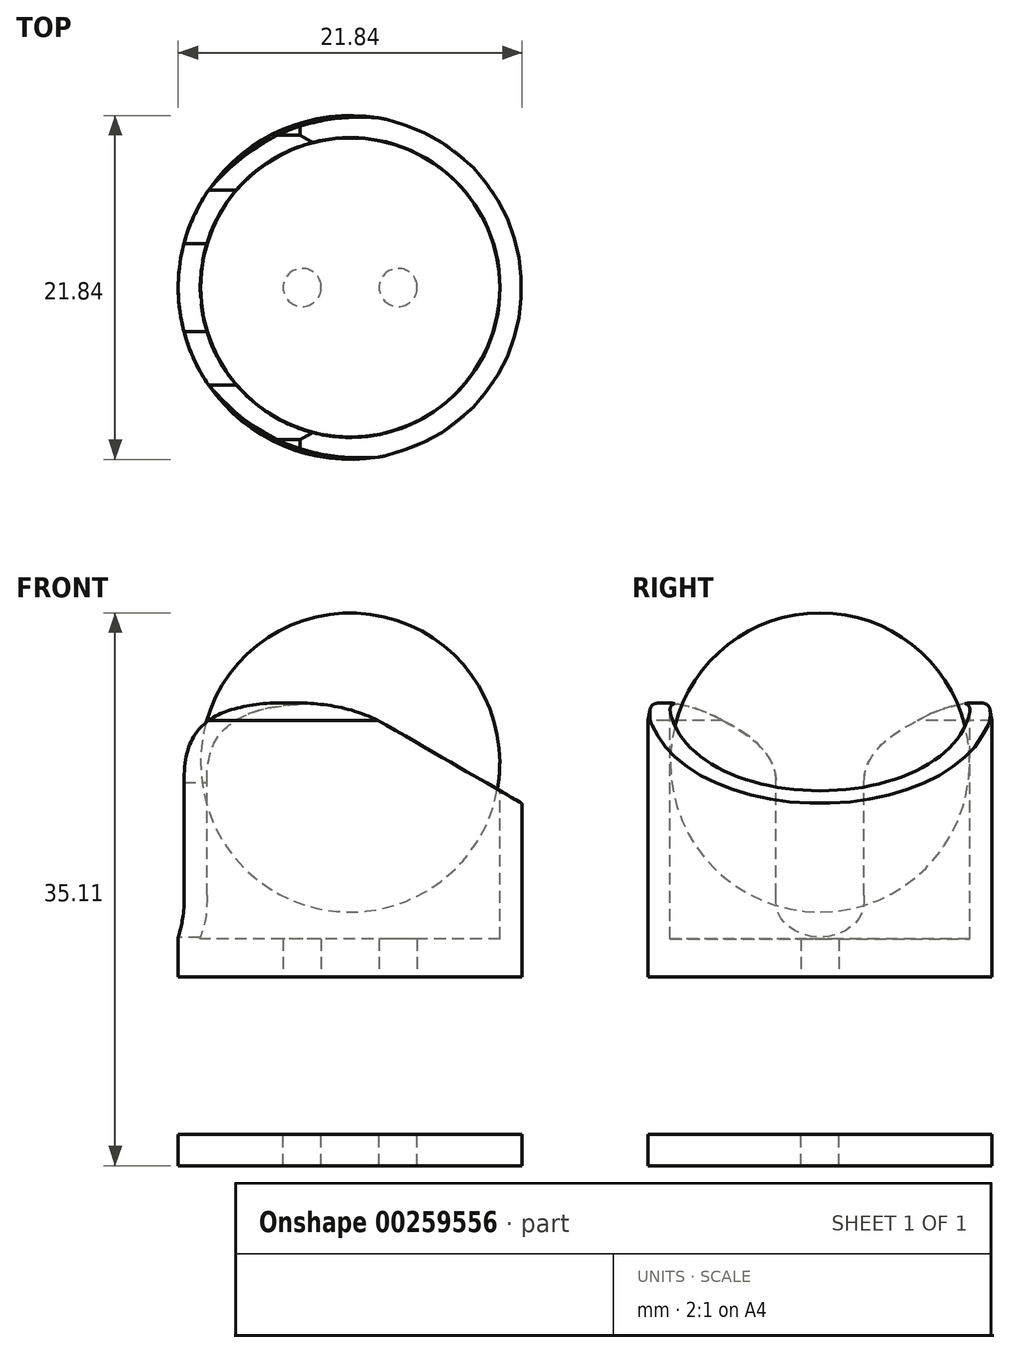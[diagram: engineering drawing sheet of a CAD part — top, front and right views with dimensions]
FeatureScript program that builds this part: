
annotation { "Feature Type Name" : "Feature", "Feature Type Description" : "" }
export const myFeature = defineFeature(function(context is Context, id is Id, definition is map)
    precondition{}
    {
        {
            var Q0;
            Q0=qCreatedBy(makeId("Top.planeOp"),FACE);
            var sketch = newSketch(context, id + "F0", { "sketchPlane" : qUnion([Q0])});
            skCircle(sketch, "E0", {"center": v(0, 0) * mm, "radius": 10.92 * mm});
            skCircle(sketch, "E1", {"center": v(-3.05, 0) * mm, "radius": 1.2 * mm});
            skCircle(sketch, "E2", {"center": v(3.05, 0) * mm, "radius": 1.2 * mm});
            skSolve(sketch);
        }
        {
            var Q0;
            Q0=makeQuery(id+"F0.imprint","IMPRINT",FACE,{"disambiguationData":[TD([[makeQuery(id+"F0.imprint","IMPRINT",EDGE,{"derivedFrom":sQuery(id+"F0.wireOp",EDGE,"E0")}),1.0]])]});
            extrude(context, id + "F1", {"entities" : qUnion([Q0]), "depth" : 17.4 * mm});
        }
        {
            var Q0;
            Q0=qCreatedBy(makeId("Front.planeOp"),FACE);
            var sketch = newSketch(context, id + "F2", { "sketchPlane" : qUnion([Q0])});
            skLineSegment(sketch, "E3.0", {"start": v(-10.92, 0) * mm, "end": v(10.92, 0) * mm});
            skLineSegment(sketch, "E4", {"start": v(10.92, 0) * mm, "end": v(10.92, 11) * mm});
            skLineSegment(sketch, "E5", {"start": v(10.92, 11) * mm, "end": v(2.26, 16) * mm});
            skLineSegment(sketch, "E6", {"start": v(-10.92, 0) * mm, "end": v(-10.92, 2.52) * mm});
            skFitSpline(sketch, "E7", {"points": [v(-10.92, 2.52) * mm, v(-10.63, 3.75) * mm, v(-10.56, 5.17) * mm], "startDerivative": vector(0.7, 2.47) * mm, "endDerivative": vector(0, 2.82) * mm});
            skLineSegment(sketch, "E8", {"start": v(-10.56, 5.17) * mm, "end": v(-10.56, 12.35) * mm});
            skFitSpline(sketch, "E9", {"points": [v(-10.56, 12.35) * mm, v(-9.97, 15.2) * mm, v(-7.3, 17.04) * mm, v(-0.9, 17.16) * mm, v(2.26, 16) * mm], "startDerivative": vector(0, 14.16) * mm, "endDerivative": vector(11.3, -6.52) * mm});
            skSolve(sketch);
        }
        {
            var Q0;
            Q0=makeQuery(id+"F1.opExtrude","CAP_EDGE",EDGE,{"disambiguationData":[OSD([sQuery(id+"F0.wireOp",EDGE,"E0")])],"isStart":false});
            chamfer(context, id + "F3", {"entities" : qUnion([Q0]), "chamferType" : ChamferType.OFFSET_ANGLE, "width" : 0.2 * mm, "oppositeDirection" : false, "angle" : 80 * degree, "tangentPropagation" : true});
        }
        {
            var Q0;
            Q0 = qSketchRegion(id + "F2", true);
            extrude(context, id + "F4", {"entities" : qUnion([Q0]), "operationType" : NewBodyOperationType.INTERSECT, "endBound" : BoundingType.SYMMETRIC, "oppositeDirection" : true, "depth" : 25 * mm});
        }
        {
            var Q0;
            Q0=makeQuery(id+"F1.opExtrude","CAP_EDGE",EDGE,{"disambiguationData":[OSD([sQuery(id+"F0.wireOp",EDGE,"E1")])],"isStart":false});
            cPoint(context, id + "F5", {"entities" : qUnion([Q0]), "parameter" : 0.5});
        }
        {
            var Q0;
            Q0=qCreatedBy(makeId("Top.planeOp"),FACE);
            var Q1;
            Q1 = qCreatedBy(id + "F5" ,VERTEX);
            cPlane(context, id + "F6", {"entities" : qUnion([Q0, Q1]), "cplaneType" : CPlaneType.PLANE_POINT, "offset" : 25 * mm, "width" : 150 * mm, "height" : 150 * mm});
        }
        {
            var Q0;
            Q0=qCreatedBy(id+"F6.planeOp",FACE);
            var sketch = newSketch(context, id + "F7", { "sketchPlane" : qUnion([Q0])});
            skCircle(sketch, "E10", {"center": v(0, 0) * mm, "radius": 9.52 * mm});
            skSolve(sketch);
        }
        {
            var Q0;
            Q0 = qSketchRegion(id + "F7", true);
            extrude(context, id + "F8", {"entities" : qUnion([Q0]), "operationType" : NewBodyOperationType.REMOVE, "oppositeDirection" : true, "depth" : 15 * mm});
        }
        {
            var Q0;
            Q0=qCreatedBy(makeId("Right.planeOp"),FACE);
            var sketch = newSketch(context, id + "F9", { "sketchPlane" : qUnion([Q0])});
            skLineSegment(sketch, "E11.0", {"start": v(-2.8, 12.35) * mm, "end": v(-2.8, 5.17) * mm});
            skFitSpline(sketch, "E11.1", {"points": [v(-2.8, 5.17) * mm, v(-2.8, 4.99) * mm, v(-2.8, 4.62) * mm, v(-2.7, 4.17) * mm, v(-2.56, 3.84) * mm, v(-2.4, 3.6) * mm, v(-2.23, 3.4) * mm, v(-1.95, 3.16) * mm, v(-1.58, 2.92) * mm, v(-1.07, 2.7) * mm, v(-0.55, 2.56) * mm, v(0, 2.5) * mm, v(0.54, 2.56) * mm, v(1.08, 2.7) * mm, v(1.57, 2.91) * mm, v(1.96, 3.16) * mm, v(2.23, 3.4) * mm, v(2.41, 3.6) * mm, v(2.56, 3.83) * mm, v(2.67, 4.09) * mm, v(2.74, 4.35) * mm, v(2.8, 4.71) * mm, v(2.8, 4.99) * mm, v(2.8, 5.17) * mm]});
            skLineSegment(sketch, "E11.2", {"start": v(2.8, 5.17) * mm, "end": v(2.8, 12.35) * mm});
            skPoint(sketch, "E11.3", {"position": v(-2.8, 8.76) * mm});
            skFitSpline(sketch, "E12.0", {"points": [v(2.8, 12.35) * mm, v(2.8, 12.6) * mm, v(2.84, 12.95) * mm, v(2.99, 13.4) * mm, v(3.14, 13.73) * mm, v(3.32, 14.04) * mm, v(3.6, 14.42) * mm, v(4, 14.84) * mm, v(4.53, 15.27) * mm, v(5.27, 15.78) * mm, v(5.82, 16.08) * mm, v(6.2, 16.27) * mm]});
            skFitSpline(sketch, "E12.1", {"points": [v(9.66, 17.4) * mm, v(9.46, 17.38) * mm, v(9, 17.32) * mm, v(8.17, 17.12) * mm, v(7.2, 16.79) * mm, v(6.53, 16.47) * mm, v(6.2, 16.27) * mm]});
            skFitSpline(sketch, "E12.2", {"points": [v(-6.2, 16.27) * mm, v(-5.82, 16.08) * mm, v(-5.27, 15.78) * mm, v(-4.54, 15.28) * mm, v(-4.02, 14.84) * mm, v(-3.53, 14.34) * mm, v(-3.2, 13.85) * mm, v(-3, 13.42) * mm, v(-2.84, 12.95) * mm, v(-2.8, 12.6) * mm, v(-2.8, 12.35) * mm]});
            skFitSpline(sketch, "E12.3", {"points": [v(-6.2, 16.27) * mm, v(-6.53, 16.47) * mm, v(-7.2, 16.79) * mm, v(-8, 17.06) * mm, v(-8.58, 17.22) * mm, v(-9.1, 17.33) * mm, v(-9.46, 17.38) * mm, v(-9.66, 17.4) * mm]});
            skLineSegment(sketch, "E13", {"start": v(9.66, 17.4) * mm, "end": v(-9.66, 17.4) * mm});
            skSolve(sketch);
        }
        {
            var Q0;
            Q0 = qSketchRegion(id + "F9", true);
            extrude(context, id + "F10", {"entities" : qUnion([Q0]), "operationType" : NewBodyOperationType.REMOVE, "oppositeDirection" : true, "depth" : 25 * mm});
        }
        {
            var Q0;
            Q0=qCreatedBy(makeId("Top.planeOp"),FACE);
            cPlane(context, id + "F11", {"entities" : qUnion([Q0]), "cplaneType" : CPlaneType.OFFSET, "offset" : 13.6 * mm, "width" : 150 * mm, "height" : 150 * mm});
        }
        {
            var Q0;
            Q0=qCreatedBy(id+"F11.planeOp",FACE);
            var sketch = newSketch(context, id + "F12", { "sketchPlane" : qUnion([Q0])});
            skArc(sketch, "E14", {"start": v(0, 9.5) * mm, "mid": v(9.5, 0) * mm, "end": v(0, -9.5) * mm});
            skLineSegment(sketch, "E15", {"start": v(0, 9.5) * mm, "end": v(0, -9.5) * mm});
            skSolve(sketch);
        }
        {
            var Q0;
            Q0 = qSketchRegion(id + "F12", true);
            var Q1;
            Q1=sQuery(id+"F12.wireOp",EDGE,"E15");
            revolve(context, id + "F13", {"entities" : qUnion([Q0]), "axis" : qUnion([Q1]), "revolveType" : RevolveType.FULL});
        }
        {
            var Q0;
            Q0=makeQuery(id+"F1.opExtrude","CAP_FACE",FACE,{"disambiguationData":[OSD([sQuery(id+"F0.wireOp",EDGE,"E0"),sQuery(id+"F0.wireOp",EDGE,"E1"),sQuery(id+"F0.wireOp",EDGE,"E2")])],"isStart":true});
            cPlane(context, id + "F14", {"entities" : qUnion([Q0]), "cplaneType" : CPlaneType.OFFSET, "offset" : 10 * mm, "width" : 150 * mm, "height" : 150 * mm});
        }
        {
            var Q0;
            Q0=qCreatedBy(id+"F14.planeOp",FACE);
            var sketch = newSketch(context, id + "F15", { "sketchPlane" : qUnion([Q0])});
            skCircle(sketch, "E16.0", {"center": v(0, 0) * mm, "radius": 10.92 * mm});
            skCircle(sketch, "E16.1", {"center": v(3.05, 0) * mm, "radius": 1.2 * mm});
            skCircle(sketch, "E16.2", {"center": v(-3.05, 0) * mm, "radius": 1.2 * mm});
            skSolve(sketch);
        }
        {
            var Q0;
            Q0 = qSketchRegion(id + "F15", true);
            extrude(context, id + "F16", {"entities" : qUnion([Q0]), "depth" : 2 * mm});
        }
    });
